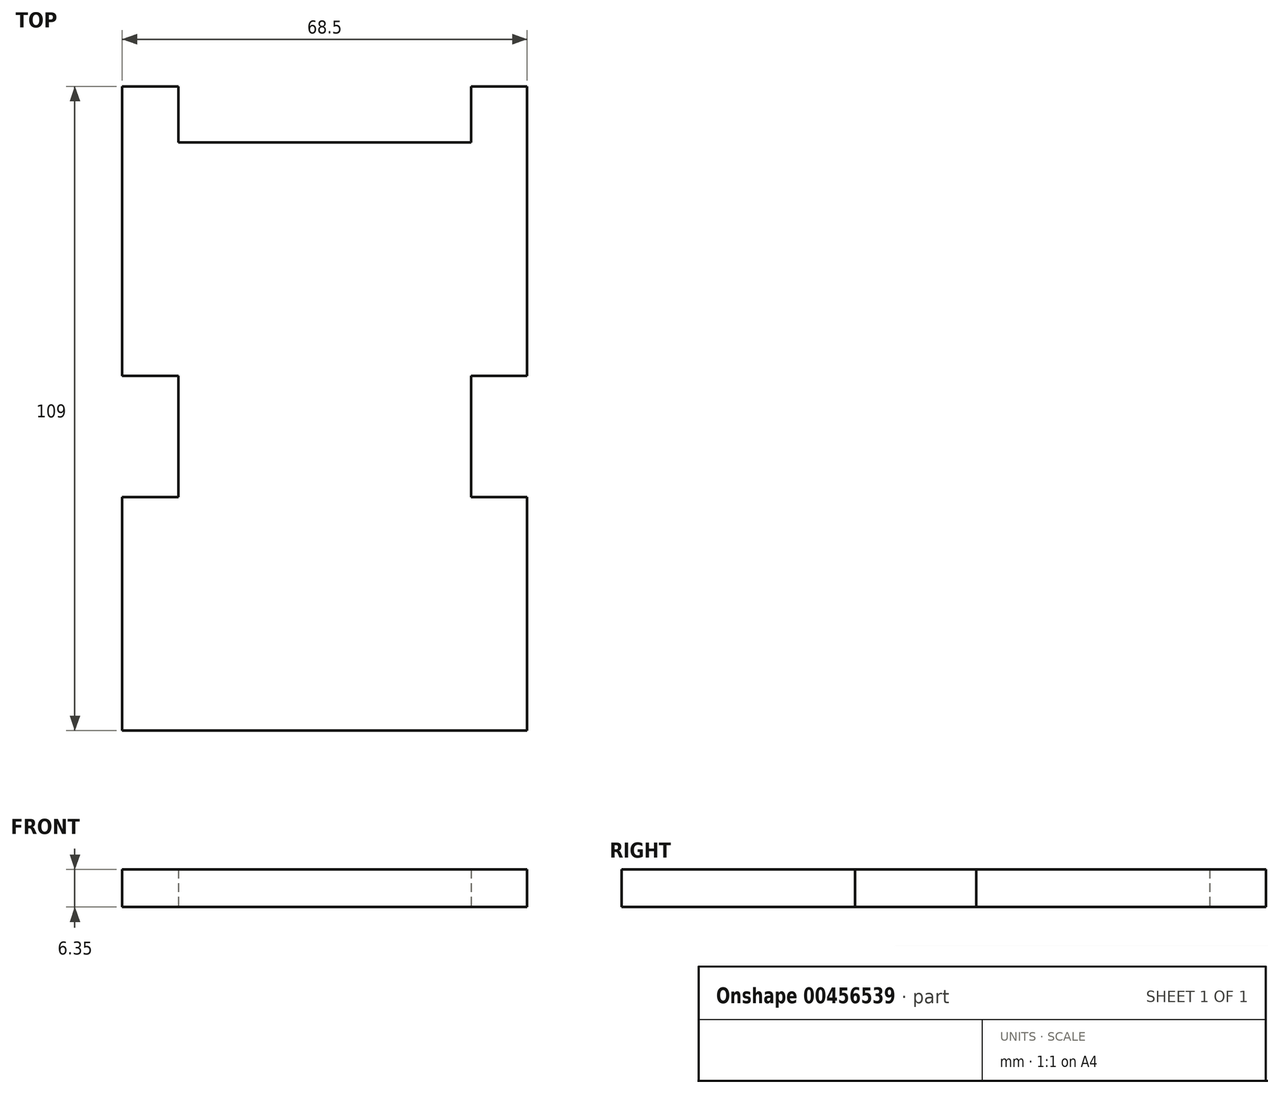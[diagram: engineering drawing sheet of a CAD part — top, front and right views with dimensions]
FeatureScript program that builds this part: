
annotation { "Feature Type Name" : "Feature", "Feature Type Description" : "" }
export const myFeature = defineFeature(function(context is Context, id is Id, definition is map)
    precondition{}
    {
        {
            var Q0;
            Q0=qCreatedBy(makeId("Top.planeOp"),FACE);
            var sketch = newSketch(context, id + "F0", { "sketchPlane" : qUnion([Q0])});
            skLineSegment(sketch, "E0.bottom", {"start": v(-24.75, 49.75) * mm, "end": v(24.75, 49.75) * mm});
            skLineSegment(sketch, "E0.top", {"start": v(-24.75, -49.75) * mm, "end": v(24.75, -49.75) * mm});
            skLineSegment(sketch, "E0.left", {"start": v(-24.75, 49.75) * mm, "end": v(-24.75, -49.75) * mm});
            skLineSegment(sketch, "E0.right", {"start": v(24.75, 49.75) * mm, "end": v(24.75, -49.75) * mm});
            skPoint(sketch, "E0.middle", {"position": v(0, 0) * mm});
            skLineSegment(sketch, "E1.bottom", {"start": v(-24.75, 49.75) * mm, "end": v(-34.25, 49.75) * mm});
            skLineSegment(sketch, "E1.top", {"start": v(-24.75, 10.25) * mm, "end": v(-34.25, 10.25) * mm});
            skLineSegment(sketch, "E1.left", {"start": v(-24.75, 49.75) * mm, "end": v(-24.75, 10.25) * mm});
            skLineSegment(sketch, "E1.right", {"start": v(-34.25, 49.75) * mm, "end": v(-34.25, 10.25) * mm});
            skLineSegment(sketch, "E2.bottom", {"start": v(-24.75, -49.75) * mm, "end": v(-34.25, -49.75) * mm});
            skLineSegment(sketch, "E2.top", {"start": v(-24.75, -10.25) * mm, "end": v(-34.25, -10.25) * mm});
            skLineSegment(sketch, "E2.left", {"start": v(-24.75, -49.75) * mm, "end": v(-24.75, -10.25) * mm});
            skLineSegment(sketch, "E2.right", {"start": v(-34.25, -49.75) * mm, "end": v(-34.25, -10.25) * mm});
            skLineSegment(sketch, "E3.bottom", {"start": v(-24.75, 49.75) * mm, "end": v(-10.25, 49.75) * mm});
            skLineSegment(sketch, "E3.top", {"start": v(-24.75, 59.25) * mm, "end": v(-10.25, 59.25) * mm});
            skLineSegment(sketch, "E3.left", {"start": v(-24.75, 49.75) * mm, "end": v(-24.75, 59.25) * mm});
            skLineSegment(sketch, "E3.right", {"start": v(-10.25, 49.75) * mm, "end": v(-10.25, 59.25) * mm});
            skLineSegment(sketch, "E4.bottom", {"start": v(24.75, 49.75) * mm, "end": v(10.25, 49.75) * mm});
            skLineSegment(sketch, "E4.top", {"start": v(24.75, 59.25) * mm, "end": v(10.25, 59.25) * mm});
            skLineSegment(sketch, "E4.left", {"start": v(24.75, 49.75) * mm, "end": v(24.75, 59.25) * mm});
            skLineSegment(sketch, "E4.right", {"start": v(10.25, 49.75) * mm, "end": v(10.25, 59.25) * mm});
            skLineSegment(sketch, "E5.bottom", {"start": v(-24.75, -49.75) * mm, "end": v(-10.25, -49.75) * mm});
            skLineSegment(sketch, "E5.top", {"start": v(-24.75, -59.25) * mm, "end": v(-10.25, -59.25) * mm});
            skLineSegment(sketch, "E5.left", {"start": v(-24.75, -49.75) * mm, "end": v(-24.75, -59.25) * mm});
            skLineSegment(sketch, "E5.right", {"start": v(-10.25, -49.75) * mm, "end": v(-10.25, -59.25) * mm});
            skLineSegment(sketch, "E6.bottom", {"start": v(24.75, -49.75) * mm, "end": v(10.25, -49.75) * mm});
            skLineSegment(sketch, "E6.top", {"start": v(24.75, -59.25) * mm, "end": v(10.25, -59.25) * mm});
            skLineSegment(sketch, "E6.left", {"start": v(24.75, -49.75) * mm, "end": v(24.75, -59.25) * mm});
            skLineSegment(sketch, "E6.right", {"start": v(10.25, -49.75) * mm, "end": v(10.25, -59.25) * mm});
            skLineSegment(sketch, "E7.bottom", {"start": v(24.75, 49.75) * mm, "end": v(34.25, 49.75) * mm});
            skLineSegment(sketch, "E7.top", {"start": v(24.75, 10.25) * mm, "end": v(34.25, 10.25) * mm});
            skLineSegment(sketch, "E7.left", {"start": v(24.75, 49.75) * mm, "end": v(24.75, 10.25) * mm});
            skLineSegment(sketch, "E7.right", {"start": v(34.25, 49.75) * mm, "end": v(34.25, 10.25) * mm});
            skLineSegment(sketch, "E8.bottom", {"start": v(24.75, -49.75) * mm, "end": v(34.25, -49.75) * mm});
            skLineSegment(sketch, "E8.top", {"start": v(24.75, -10.25) * mm, "end": v(34.25, -10.25) * mm});
            skLineSegment(sketch, "E8.left", {"start": v(24.75, -49.75) * mm, "end": v(24.75, -10.25) * mm});
            skLineSegment(sketch, "E8.right", {"start": v(34.25, -49.75) * mm, "end": v(34.25, -10.25) * mm});
            skLineSegment(sketch, "E9.bottom", {"start": v(24.75, 59.25) * mm, "end": v(34.25, 59.25) * mm});
            skLineSegment(sketch, "E9.left", {"start": v(24.75, 59.25) * mm, "end": v(24.75, 49.75) * mm});
            skLineSegment(sketch, "E9.right", {"start": v(34.25, 59.25) * mm, "end": v(34.25, 49.75) * mm});
            skLineSegment(sketch, "E10.bottom", {"start": v(-24.75, 59.25) * mm, "end": v(-34.25, 59.25) * mm});
            skLineSegment(sketch, "E10.left", {"start": v(-24.75, 59.25) * mm, "end": v(-24.75, 49.75) * mm});
            skLineSegment(sketch, "E10.right", {"start": v(-34.25, 59.25) * mm, "end": v(-34.25, 49.75) * mm});
            skLineSegment(sketch, "E11.bottom", {"start": v(-34.25, -49.75) * mm, "end": v(-24.75, -49.75) * mm});
            skLineSegment(sketch, "E11.top", {"start": v(-34.25, -59.25) * mm, "end": v(-24.75, -59.25) * mm});
            skLineSegment(sketch, "E11.left", {"start": v(-34.25, -49.75) * mm, "end": v(-34.25, -59.25) * mm});
            skLineSegment(sketch, "E12.bottom", {"start": v(34.25, -49.75) * mm, "end": v(24.75, -49.75) * mm});
            skLineSegment(sketch, "E12.top", {"start": v(34.25, -59.25) * mm, "end": v(24.75, -59.25) * mm});
            skLineSegment(sketch, "E12.left", {"start": v(34.25, -49.75) * mm, "end": v(34.25, -59.25) * mm});
            skSolve(sketch);
        }
        {
            var Q0;
            Q0=makeQuery(id+"F0.imprint","IMPRINT",FACE,{"disambiguationData":[TD([[makeQuery(id+"F0.imprint","IMPRINT",EDGE,{"derivedFrom":sQuery(id+"F0.wireOp",EDGE,"E3.bottom")}),1.0]])]});
            var Q1;
            Q1=makeQuery(id+"F0.imprint","IMPRINT",FACE,{"disambiguationData":[TD([[makeQuery(id+"F0.imprint","IMPRINT",EDGE,{"derivedFrom":sQuery(id+"F0.wireOp",EDGE,"E10.bottom")}),1.0]])]});
            var Q2;
            Q2=makeQuery(id+"F0.imprint","IMPRINT",FACE,{"disambiguationData":[TD([[makeQuery(id+"F0.imprint","IMPRINT",EDGE,{"derivedFrom":sQuery(id+"F0.wireOp",EDGE,"E1.top")}),-1.0]])]});
            var Q3;
            Q3=makeQuery(id+"F0.imprint","IMPRINT",FACE,{"disambiguationData":[TD([[makeQuery(id+"F0.imprint","IMPRINT",EDGE,{"derivedFrom":sQuery(id+"F0.wireOp",EDGE,"E4.bottom")}),-1.0]])]});
            var Q4;
            Q4=makeQuery(id+"F0.imprint","IMPRINT",FACE,{"disambiguationData":[TD([[makeQuery(id+"F0.imprint","IMPRINT",EDGE,{"derivedFrom":sQuery(id+"F0.wireOp",EDGE,"E9.bottom")}),-1.0]])]});
            var Q5;
            Q5=makeQuery(id+"F0.imprint","IMPRINT",FACE,{"disambiguationData":[TD([[makeQuery(id+"F0.imprint","IMPRINT",EDGE,{"derivedFrom":sQuery(id+"F0.wireOp",EDGE,"E7.top")}),1.0]])]});
            var Q6;
            Q6=makeQuery(id+"F0.imprint","IMPRINT",FACE,{"disambiguationData":[TD([[makeQuery(id+"F0.imprint","IMPRINT",EDGE,{"derivedFrom":sQuery(id+"F0.wireOp",EDGE,"E8.top")}),-1.0]])]});
            var Q7;
            Q7=makeQuery(id+"F0.imprint","IMPRINT",FACE,{"disambiguationData":[TD([[makeQuery(id+"F0.imprint","IMPRINT",EDGE,{"derivedFrom":sQuery(id+"F0.wireOp",EDGE,"E12.bottom")}),1.0]])]});
            var Q8;
            Q8=makeQuery(id+"F0.imprint","IMPRINT",FACE,{"disambiguationData":[TD([[makeQuery(id+"F0.imprint","IMPRINT",EDGE,{"derivedFrom":sQuery(id+"F0.wireOp",EDGE,"E6.bottom")}),1.0]])]});
            var Q9;
            Q9=makeQuery(id+"F0.imprint","IMPRINT",FACE,{"disambiguationData":[TD([[makeQuery(id+"F0.imprint","IMPRINT",EDGE,{"derivedFrom":sQuery(id+"F0.wireOp",EDGE,"E5.bottom")}),-1.0]])]});
            var Q10;
            Q10=makeQuery(id+"F0.imprint","IMPRINT",FACE,{"disambiguationData":[TD([[makeQuery(id+"F0.imprint","IMPRINT",EDGE,{"derivedFrom":sQuery(id+"F0.wireOp",EDGE,"E11.bottom")}),-1.0]])]});
            var Q11;
            Q11=makeQuery(id+"F0.imprint","IMPRINT",FACE,{"disambiguationData":[TD([[makeQuery(id+"F0.imprint","IMPRINT",EDGE,{"derivedFrom":sQuery(id+"F0.wireOp",EDGE,"E2.top")}),1.0]])]});
            var Q12;
            Q12=makeQuery(id+"F0.imprint","IMPRINT",FACE,{"disambiguationData":[TD([[makeQuery(id+"F0.imprint","IMPRINT",EDGE,{"derivedFrom":sQuery(id+"F0.wireOp",EDGE,"E0.bottom")}),-1.0]])]});
            extrude(context, id + "F1", {"entities" : qUnion([Q0, Q1, Q2, Q3, Q4, Q5, Q6, Q7, Q8, Q9, Q10, Q11, Q12]), "depth" : 6.35 * mm});
        }
    });
